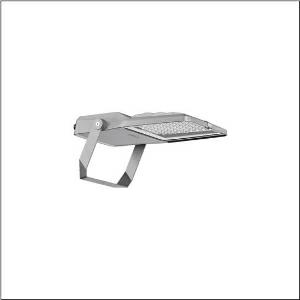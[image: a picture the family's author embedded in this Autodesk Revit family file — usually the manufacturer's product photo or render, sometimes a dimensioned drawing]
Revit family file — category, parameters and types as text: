
# Revit family: floodlight_fl_21_mini___pl61_5xa7776c4c1a_3fb0
name_source: partatom
category: Lighting Fixtures
units: mm (PartAtom-declared; Revit-internal decimal feet)

## family parameters
Cut with Voids When Loaded = No
Host = Face
Light Source = No
Part Type = Normal
Room Calculation Point = No
Round Connector Dimension = Use Diameter
Shared = No

## types (1)
- --- (1 x LED, 12460 lm, 89 W, 4000K)
    Apparent Load = 89 VA
    CIE Flux Codes = 33 65 98 100 100
    Color Rendering = 70
    Color Temperature = 4000K
    Default Elevation = 1800 mm
    Description = Floodlight FL 21 mini, floodlight, primary light control with lens, of PMMA, primary optical cover: protective disc, of toughened safety glass, transparent, light distribution: PL61, light emission: direct distribution, installation type: surface-mounted, LED, High Power LED, rated luminous flux: 12.460lm, luminous efficacy: 140lm/W, light colour: 740, colour temperature: 4000K, control gear: D4iSmart Interface (Zhaga), control: overheat protection, constant luminous flux control, time-dependent luminous flux control, flexible luminous flux parameterisation, pre-setting: logarithmic dimming characteristic, with terminal, 6-pole, mains connection: 220..240V, AC, 50/60Hz, start of lifetime: 89W, end of service life: 94W, reduction: 43W, mounting bracket, of diecast aluminium, powder-coated, Siteco® metallic grey (DB 702S), corrosivity category C5 mid according to DIN EN ISO 12944, suitable for swimming pools, chlorine-resistant, sealing non-destructively replaceable, mounting bracket, of steel, galvanised, powder-coated, Siteco® metallic grey (DB 702S), Smart Interface below and above, protection rating (complete): IP66, insulation class (complete): insulation class II (safety insulation), certification: CE, ENEC, VDE, protection symbol: D, impact resistance: IK08, permissible operating ambient temperature: -40..+40°C, permissible operating ambient temperature for outdoor applications: -40..+50°C, standard: DIN EN 12944, LABS conformity tested according to VDMA 24364:2018-05, packaging unit: 1 piece

Light Distribution: PL61
    Height = 70 mm
    Lamp = 1 x LED
    Lamp Light Flux = 12460 lm
    Lamp Power = 89 W
    Lamp count = 1
    Length = 485 mm
    Luminous efficacy = 140 lm/W
    Manufacturer = Siteco
    ModVariant = No
    Model = 5XA7776C4C1A
    Number of Poles = 1
    OnlyDefault = Yes
    Power Factor = 1
    Product Name = Floodlight FL 21 mini | PL61
    Product group = floodlight | pylon annexe
    ProductGroupID = 6200
    Protection Class = Protection class II
    Protection Degree = IP 66
    RLX_Detail_Level = 1
    RLX_Emergency_Light_Flux = 0 lm
    RLX_Emergency_Type = 0
    RLX_Emergency_Type_DB = No
    RlxData = <blob elided: 95949 chars, md5=ebebb2aa>
    Socket = socket
    Standby Power = 0 W
    System Light Flux = 12460 lm
    System Power = 89 W
    Type Comments = factory setting: luminous flux: 100 % | dim-lin: 254 | 456 mA
    Type Image = l_1006845.jpg
    URL = http://relux.com
    VarID = @adj_100580
    Voltage = 0 V
    Weight = 0.00 kg
    Width = 337 mm

## geometry (parser evidence)
native form markers: Blend x4, Sweep x12
no freeform markers — native parametric forms only
